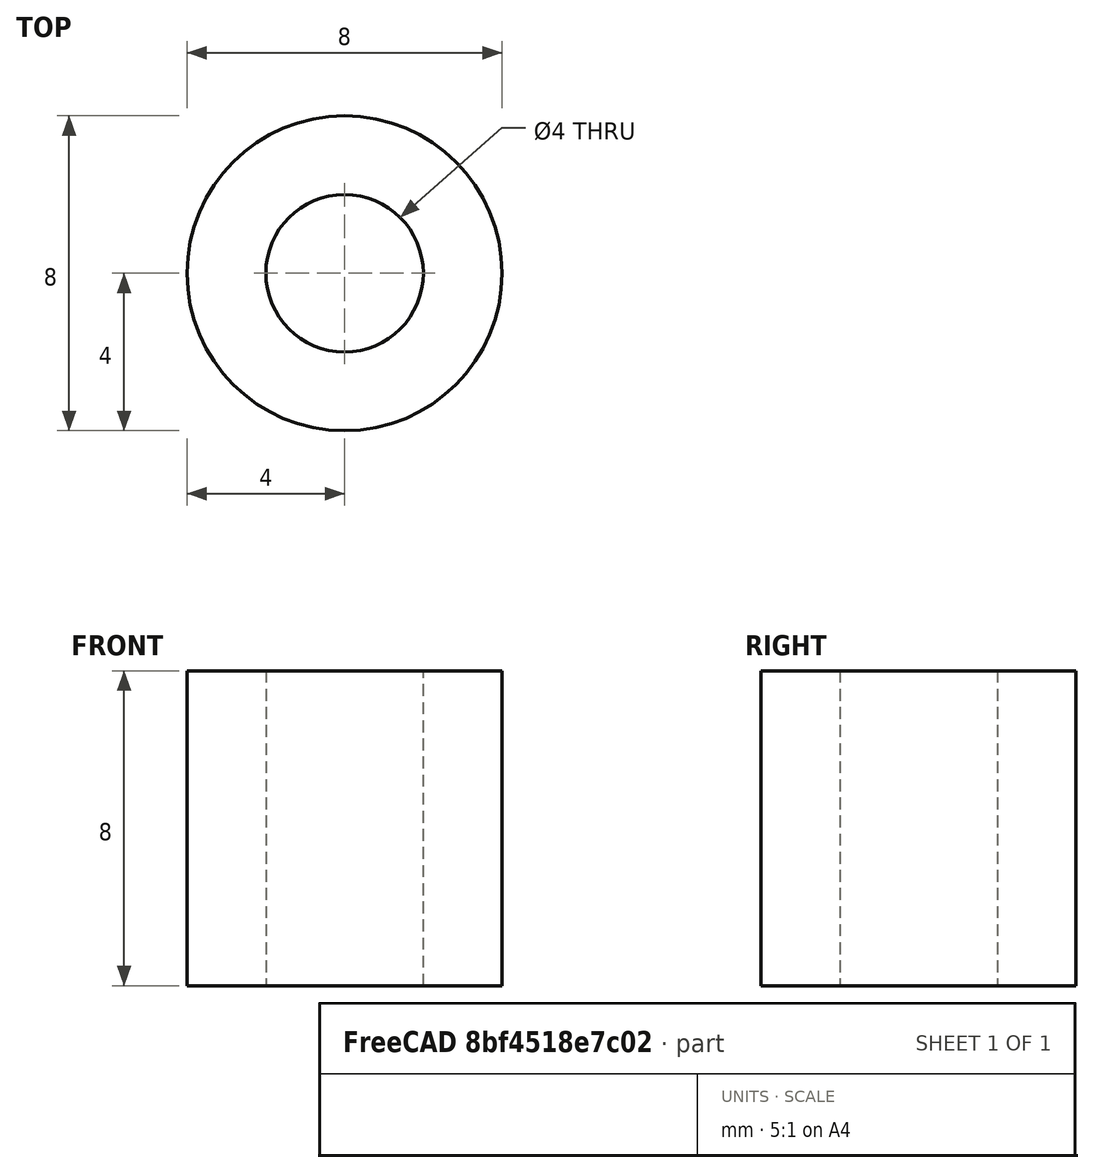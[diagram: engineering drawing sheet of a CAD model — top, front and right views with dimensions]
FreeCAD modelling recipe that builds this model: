
FCSTD DOCUMENT  (FreeCAD 0.20R27319 (Git))
Label: Centre
License: All rights reserved
LicenseURL: http://en.wikipedia.org/wiki/All_rights_reserved
objects: Sketcher::SketchObject×1, PartDesign::Pad×1, PartDesign::Body×1
note: 4 computed .brp shape members not serialized (recipe doc carries the construction recipe); baked Part::Feature solids carry a one-line shape summary decoded from their .brp

FEATURE [Sketcher::SketchObject] Sketch
  FullyConstrained = true
  MapMode = 5
  Support = -> [XY_Plane]
  sketch-geometry (2):
    g0: Circle CenterX=0 CenterY=0 CenterZ=0 NormalX=0 NormalY=0 NormalZ=1 AngleXU=0 Radius=2
    g1: Circle CenterX=0 CenterY=0 CenterZ=0 NormalX=0 NormalY=0 NormalZ=1 AngleXU=0 Radius=4
  constraints (4):
    c: Coincident(g0,g-1)
    c: Coincident(g1,g0)
    c: Diameter(g0) = 4
    c: Diameter(g1) = 8
FEATURE [PartDesign::Pad] Pad
  Direction = (0,0,1)
  Length = 8
  Length2 = 10
  Profile = -> Sketch
  ReferenceAxis = -> Sketch [N_Axis]
  Type = 0
FEATURE [PartDesign::Body] Body
  Group = -> [Sketch,Pad]
  Origin = -> Origin
  Tip = -> Pad
